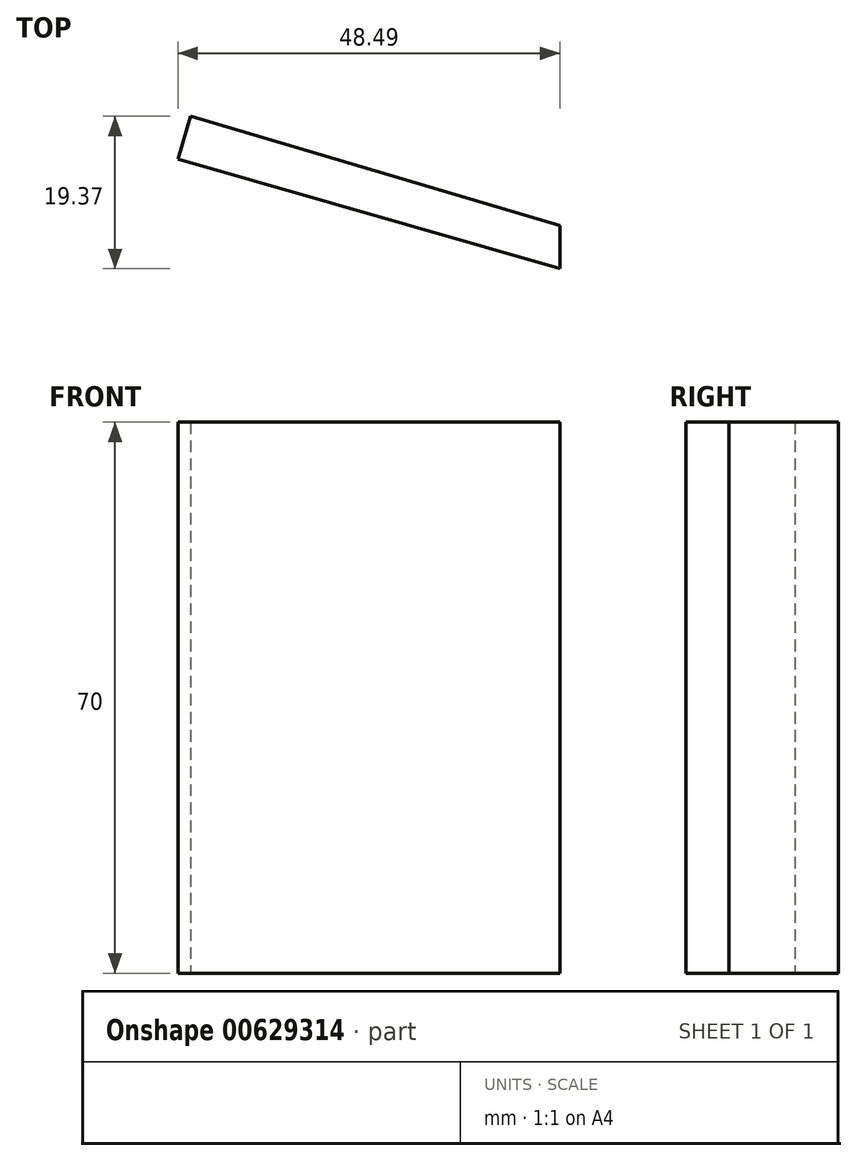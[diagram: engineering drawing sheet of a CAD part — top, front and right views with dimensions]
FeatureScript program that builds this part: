
annotation { "Feature Type Name" : "Feature", "Feature Type Description" : "" }
export const myFeature = defineFeature(function(context is Context, id is Id, definition is map)
    precondition{}
    {
        {
            var Q0;
            Q0=qCreatedBy(makeId("Top.planeOp"),FACE);
            var sketch = newSketch(context, id + "F0", { "sketchPlane" : qUnion([Q0])});
            skLineSegment(sketch, "E0.bottom", {"start": v(-38.06, 17.3) * mm, "end": v(-33.06, 17.3) * mm});
            skLineSegment(sketch, "E0.top", {"start": v(-38.06, -42.7) * mm, "end": v(-33.06, -42.7) * mm});
            skLineSegment(sketch, "E0.left", {"start": v(-38.06, 17.3) * mm, "end": v(-38.06, -42.7) * mm});
            skLineSegment(sketch, "E0.right", {"start": v(-33.06, 17.3) * mm, "end": v(-33.06, -42.7) * mm});
            skLineSegment(sketch, "E1", {"start": v(-61.67, 25.74) * mm, "end": v(-13.18, 11.84) * mm});
            skLineSegment(sketch, "E2", {"start": v(-61.67, 25.74) * mm, "end": v(-60.1, 31.2) * mm});
            skLineSegment(sketch, "E3", {"start": v(-60.1, 31.2) * mm, "end": v(-13.18, 17.3) * mm});
            skLineSegment(sketch, "E4", {"start": v(-13.18, 17.3) * mm, "end": v(-13.18, 11.84) * mm});
            skLineSegment(sketch, "E5", {"start": v(-38.06, 17.3) * mm, "end": v(-43.66, 20.58) * mm});
            skArc(sketch, "E6", {"start": v(-19, -46.68) * mm, "mid": v(-42.62, -42.22) * mm, "end": v(-66.52, -44.74) * mm});
            skLineSegment(sketch, "E7", {"start": v(-66.52, -44.74) * mm, "end": v(-66.52, -40.21) * mm});
            skLineSegment(sketch, "E8", {"start": v(-66.52, -40.21) * mm, "end": v(-38.06, -37.62) * mm});
            skLineSegment(sketch, "E9", {"start": v(-38.06, -37.62) * mm, "end": v(-33.06, -36.38) * mm});
            skLineSegment(sketch, "E10", {"start": v(-19, -46.68) * mm, "end": v(-33.06, -36.38) * mm});
            skLineSegment(sketch, "E11", {"start": v(-33.06, 17.3) * mm, "end": v(-33.06, 17.54) * mm});
            skSolve(sketch);
        }
        {
            var Q0;
            {var subQ0=sQuery(id+"F0.wireOp",EDGE,"E2");Q0=makeQuery(id+"F0.imprint","IMPRINT",FACE,{"disambiguationData":[TD([[makeQuery(id+"F0.imprint","IMPRINT",EDGE,{"derivedFrom":subQ0}),-1.0]])]});}
            extrude(context, id + "F1", {"entities" : qUnion([Q0]), "depth" : 70 * mm, "offsetDistance" : 25 * mm});
        }
    });
